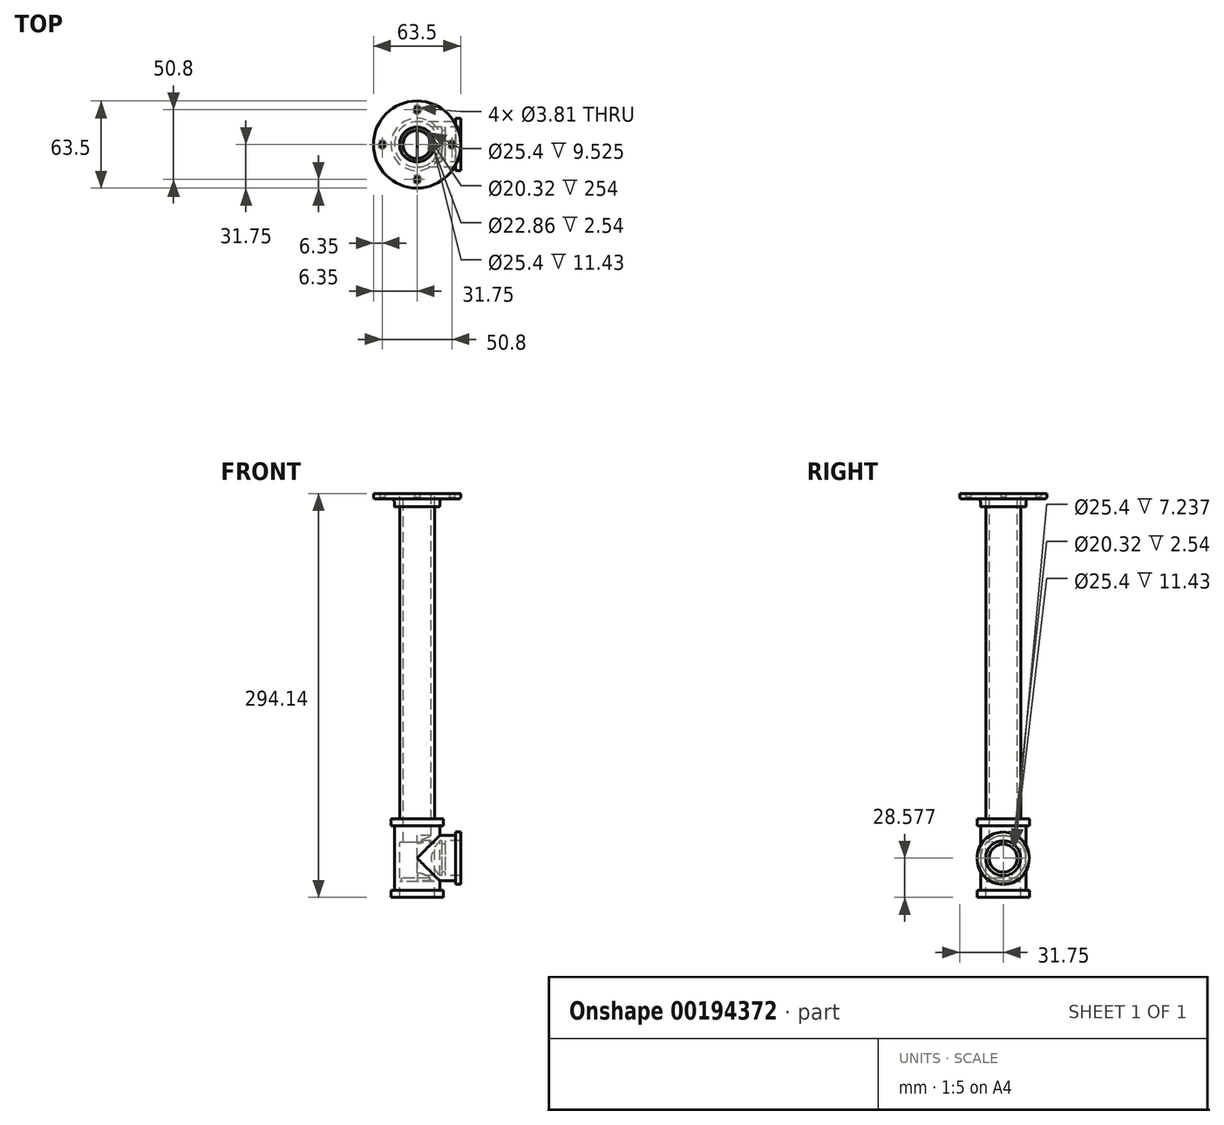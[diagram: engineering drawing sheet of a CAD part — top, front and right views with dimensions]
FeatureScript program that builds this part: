
annotation { "Feature Type Name" : "Feature", "Feature Type Description" : "" }
export const myFeature = defineFeature(function(context is Context, id is Id, definition is map)
    precondition{}
    {
        {
            var Q0;
            Q0=qCreatedBy(makeId("Front.planeOp"),FACE);
            var sketch = newSketch(context, id + "F0", { "sketchPlane" : qUnion([Q0])});
            skLineSegment(sketch, "E0", {"start": v(0, 58.7) * mm, "end": v(0, -194) * mm, "construction": true});
            skLineSegment(sketch, "E1.bottom", {"start": v(10.16, 0) * mm, "end": v(12.7, 0) * mm});
            skLineSegment(sketch, "E1.top", {"start": v(10.16, -254) * mm, "end": v(12.7, -254) * mm});
            skLineSegment(sketch, "E1.left", {"start": v(10.16, 0) * mm, "end": v(10.16, -254) * mm});
            skLineSegment(sketch, "E1.right", {"start": v(12.7, 0) * mm, "end": v(12.7, -254) * mm});
            skSolve(sketch);
        }
        {
            var Q0;
            Q0 = qSketchRegion(id + "F0", true);
            var Q1;
            Q1=sQuery(id+"F0.wireOp",EDGE,"E0");
            revolve(context, id + "F1", {"entities" : qUnion([Q0]), "axis" : qUnion([Q1]), "revolveType" : RevolveType.FULL});
        }
        {
            var Q0;
            Q0=qCreatedBy(makeId("Front.planeOp"),FACE);
            var sketch = newSketch(context, id + "F2", { "sketchPlane" : qUnion([Q0])});
            skLineSegment(sketch, "E2", {"start": v(12.7, -9.53) * mm, "end": v(12.7, 0) * mm});
            skLineSegment(sketch, "E3", {"start": v(12.7, 0) * mm, "end": v(31.75, 0) * mm});
            skLineSegment(sketch, "E4", {"start": v(31.75, 0) * mm, "end": v(31.75, -2.54) * mm});
            skLineSegment(sketch, "E5", {"start": v(30.48, -3.81) * mm, "end": v(19.05, -3.81) * mm});
            skLineSegment(sketch, "E6", {"start": v(16.51, -6.35) * mm, "end": v(16.51, -9.27) * mm});
            skLineSegment(sketch, "E7", {"start": v(16.26, -9.53) * mm, "end": v(12.7, -9.53) * mm});
            skLineSegment(sketch, "E8", {"start": v(0, 81.3) * mm, "end": v(0, -302.37) * mm, "construction": true});
            skPoint(sketch, "E9.visualSharp", {"position": v(16.51, -3.81) * mm});
            skArc(sketch, "E9.filletArc", {"start": v(19.05, -3.81) * mm, "mid": v(17.25, -4.55) * mm, "end": v(16.51, -6.35) * mm});
            skPoint(sketch, "E10.visualSharp", {"position": v(31.75, -3.81) * mm});
            skArc(sketch, "E10.filletArc", {"start": v(30.48, -3.81) * mm, "mid": v(31.38, -3.44) * mm, "end": v(31.75, -2.54) * mm});
            skPoint(sketch, "E11.visualSharp", {"position": v(16.51, -9.53) * mm});
            skArc(sketch, "E11.filletArc", {"start": v(16.26, -9.53) * mm, "mid": v(16.44, -9.45) * mm, "end": v(16.51, -9.27) * mm});
            skSolve(sketch);
        }
        {
            var Q0;
            Q0 = qSketchRegion(id + "F2", true);
            var Q1;
            Q1=sQuery(id+"F2.wireOp",EDGE,"E8");
            revolve(context, id + "F3", {"entities" : qUnion([Q0]), "axis" : qUnion([Q1]), "revolveType" : RevolveType.FULL});
        }
        {
            var Q0;
            Q0=qCreatedBy(makeId("Front.planeOp"),FACE);
            var sketch = newSketch(context, id + "F4", { "sketchPlane" : qUnion([Q0])});
            skLineSegment(sketch, "E12", {"start": v(0, 94.27) * mm, "end": v(0, -304.6) * mm, "construction": true});
            skLineSegment(sketch, "E13.bottom", {"start": v(12.7, -236.99) * mm, "end": v(19.05, -236.99) * mm});
            skLineSegment(sketch, "E13.top", {"start": v(12.7, -294.14) * mm, "end": v(19.05, -294.14) * mm});
            skLineSegment(sketch, "E13.left", {"start": v(12.7, -236.99) * mm, "end": v(12.7, -248.42) * mm});
            skLineSegment(sketch, "E13.right", {"start": v(16.51, -242.07) * mm, "end": v(16.51, -289.06) * mm});
            skLineSegment(sketch, "E14.top", {"start": v(16.51, -242.07) * mm, "end": v(19.05, -242.07) * mm});
            skLineSegment(sketch, "E14.right", {"start": v(19.05, -236.99) * mm, "end": v(19.05, -242.07) * mm});
            skLineSegment(sketch, "E15.top", {"start": v(16.51, -289.06) * mm, "end": v(19.05, -289.06) * mm});
            skLineSegment(sketch, "E15.right", {"start": v(19.05, -294.14) * mm, "end": v(19.05, -289.06) * mm});
            skLineSegment(sketch, "E16.bottom", {"start": v(12.7, -248.42) * mm, "end": v(11.46, -248.42) * mm});
            skLineSegment(sketch, "E16.top", {"start": v(12.7, -250.96) * mm, "end": v(11.43, -250.96) * mm});
            skLineSegment(sketch, "E16.right", {"start": v(11.46, -248.42) * mm, "end": v(11.43, -250.96) * mm});
            skLineSegment(sketch, "E17.bottom", {"start": v(12.7, -280.17) * mm, "end": v(11.43, -280.17) * mm});
            skLineSegment(sketch, "E17.top", {"start": v(12.7, -282.7) * mm, "end": v(11.43, -282.7) * mm});
            skLineSegment(sketch, "E17.right", {"start": v(11.43, -280.17) * mm, "end": v(11.43, -282.7) * mm});
            skLineSegment(sketch, "E18.trimOffspring", {"start": v(12.7, -282.7) * mm, "end": v(12.7, -294.14) * mm});
            skLineSegment(sketch, "E19", {"start": v(12.7, -250.96) * mm, "end": v(12.7, -280.17) * mm});
            skSolve(sketch);
        }
        {
            var Q0;
            Q0 = qSketchRegion(id + "F4", true);
            var Q1;
            Q1=sQuery(id+"F4.wireOp",EDGE,"E12");
            revolve(context, id + "F5", {"entities" : qUnion([Q0]), "axis" : qUnion([Q1]), "revolveType" : RevolveType.FULL});
        }
        {
            var Q0;
            Q0=qCreatedBy(makeId("Front.planeOp"),FACE);
            var sketch = newSketch(context, id + "F6", { "sketchPlane" : qUnion([Q0])});
            skLineSegment(sketch, "E20", {"start": v(0, -265.56) * mm, "end": v(49.2, -265.56) * mm, "construction": true});
            skLineSegment(sketch, "E21", {"start": v(0, -236.99) * mm, "end": v(0, -294.14) * mm, "construction": true});
            skLineSegment(sketch, "E22.bottom", {"start": v(0, -252.86) * mm, "end": v(17.78, -252.86) * mm});
            skLineSegment(sketch, "E22.top", {"start": v(0, -249.05) * mm, "end": v(27.94, -249.05) * mm});
            skLineSegment(sketch, "E22.left", {"start": v(0, -252.86) * mm, "end": v(0, -249.05) * mm});
            skLineSegment(sketch, "E22.right", {"start": v(31.75, -252.86) * mm, "end": v(31.75, -246.51) * mm});
            skLineSegment(sketch, "E23.top", {"start": v(31.75, -246.51) * mm, "end": v(27.94, -246.51) * mm});
            skLineSegment(sketch, "E23.right", {"start": v(27.94, -249.05) * mm, "end": v(27.94, -246.51) * mm});
            skLineSegment(sketch, "E24.top", {"start": v(17.78, -255.4) * mm, "end": v(20.32, -255.4) * mm});
            skLineSegment(sketch, "E24.left", {"start": v(17.78, -252.86) * mm, "end": v(17.78, -255.4) * mm});
            skLineSegment(sketch, "E24.right", {"start": v(20.32, -252.86) * mm, "end": v(20.32, -255.4) * mm});
            skLineSegment(sketch, "E25.trimOffspring", {"start": v(20.32, -252.86) * mm, "end": v(31.75, -252.86) * mm});
            skSolve(sketch);
        }
        {
            var Q0;
            Q0 = qSketchRegion(id + "F6", true);
            var Q1;
            Q1=sQuery(id+"F6.wireOp",EDGE,"E20");
            revolve(context, id + "F7", {"operationType" : NewBodyOperationType.ADD, "entities" : qUnion([Q0]), "axis" : qUnion([Q1]), "revolveType" : RevolveType.FULL});
        }
        {
            var Q0;
            Q0=makeQuery(id+"F3.opRevolve","SWEPT_FACE",FACE,{"disambiguationData":[OSD([sQuery(id+"F2.wireOp",EDGE,"E5")])]});
            var sketch = newSketch(context, id + "F8", { "sketchPlane" : qUnion([Q0])});
            skPoint(sketch, "E26", {"position": v(25.4, 0) * mm});
            skPoint(sketch, "E27.1.0", {"position": v(0, 25.4) * mm});
            skPoint(sketch, "E27.2.0", {"position": v(-25.4, 0) * mm});
            skPoint(sketch, "E27.center", {"position": v(0, 0) * mm});
            skLineSegment(sketch, "E27.anchor1", {"start": v(0, 0) * mm, "end": v(25.4, 0) * mm, "construction": true});
            skLineSegment(sketch, "E27.anchor2", {"start": v(0, 0) * mm, "end": v(0, -25.4) * mm, "construction": true});
            skPoint(sketch, "E28.0.3.0", {"position": v(0, -25.4) * mm});
            skSolve(sketch);
        }
        {
            var Q0;
            Q0=sQuery(id+"F8.wireOp",VERTEX,"E26");
            var Q1;
            Q1=sQuery(id+"F8.wireOp",VERTEX,"E27.1.0");
            var Q2;
            Q2=sQuery(id+"F8.wireOp",VERTEX,"E27.2.0");
            var Q3;
            Q3=sQuery(id+"F8.wireOp",VERTEX,"E28.0.3.0");
            var Q4;
            Q4=makeQuery(id+"F3.opRevolve","SWEPT_BODY",BODY,{"disambiguationData":[OSD([sQuery(id+"F2.wireOp",EDGE,"E2"),sQuery(id+"F2.wireOp",EDGE,"E3"),sQuery(id+"F2.wireOp",EDGE,"E4"),sQuery(id+"F2.wireOp",EDGE,"E5"),sQuery(id+"F2.wireOp",EDGE,"E6"),sQuery(id+"F2.wireOp",EDGE,"E7"),sQuery(id+"F2.wireOp",EDGE,"E9.filletArc"),sQuery(id+"F2.wireOp",EDGE,"E10.filletArc"),sQuery(id+"F2.wireOp",EDGE,"E11.filletArc")])]});
            hole(context, id + "F9", {"style" : HoleStyle.C_SINK, "endStyle" : HoleEndStyle.THROUGH, "holeDiameter" : 3.8 * mm, "cSinkDiameter" : 6.35 * mm, "cSinkAngle" : 90 * degree, "locations" : qUnion([Q0, Q1, Q2, Q3]), "scope" : qUnion([Q4]), "isTappedThrough" : true});
        }
    });
